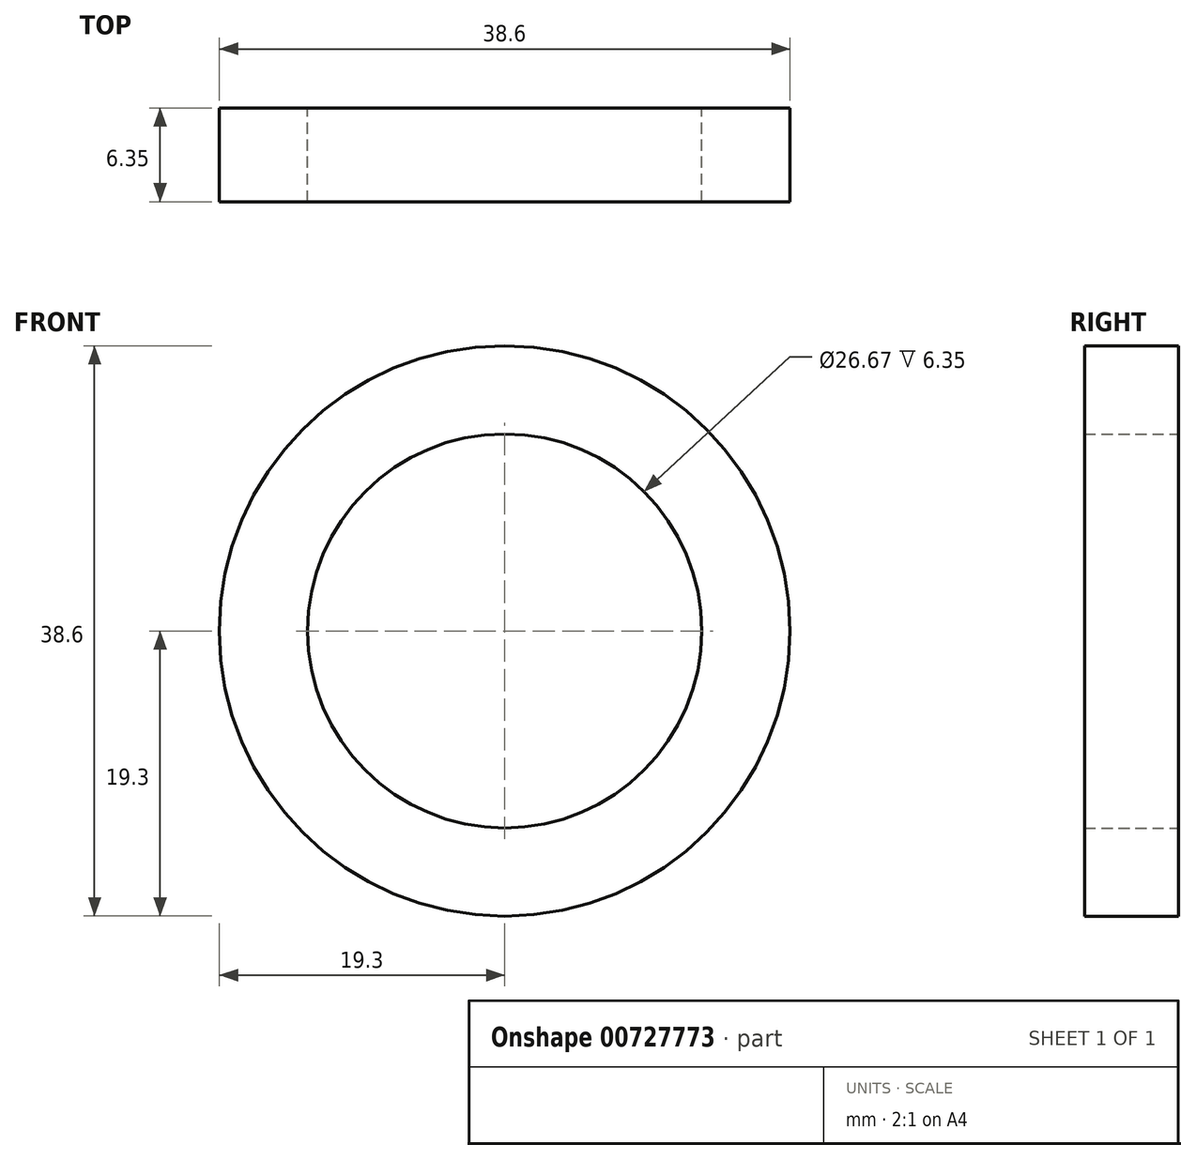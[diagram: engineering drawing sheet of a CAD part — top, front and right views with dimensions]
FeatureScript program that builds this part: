
annotation { "Feature Type Name" : "Feature", "Feature Type Description" : "" }
export const myFeature = defineFeature(function(context is Context, id is Id, definition is map)
    precondition{}
    {
        {
            var Q0;
            Q0=qCreatedBy(makeId("Front.planeOp"),FACE);
            var sketch = newSketch(context, id + "F0", { "sketchPlane" : qUnion([Q0])});
            skCircle(sketch, "E0", {"center": v(0, 0) * mm, "radius": 19.3 * mm});
            skCircle(sketch, "E1", {"center": v(0, 0) * mm, "radius": 13.34 * mm});
            skSolve(sketch);
        }
        {
            var Q0;
            Q0=makeQuery(id+"F0.imprint","IMPRINT",FACE,{"disambiguationData":[TD([[makeQuery(id+"F0.imprint","IMPRINT",EDGE,{"derivedFrom":sQuery(id+"F0.wireOp",EDGE,"E0")}),1.0]])]});
            extrude(context, id + "F1", {"entities" : qUnion([Q0]), "depth" : 6.35 * mm, "offsetDistance" : 25.4 * mm});
        }
    });
